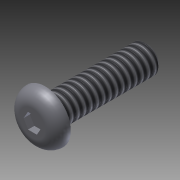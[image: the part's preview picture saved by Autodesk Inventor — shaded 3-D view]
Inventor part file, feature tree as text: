
AUTODESK INVENTOR PART (.ipt)
format: ipt  version: 2012 (Build 160160000, 160)  size: 116,736 bytes
history: native  units: in
note: dims shown in document units (in); Inventor stores cm internally (conversion verified against a paired STEP export)
features: extrude x3, sketch x1, thread x1, chamfer x1, fillet x1
ambient origin geometry x8: Origin, YZ Plane, XZ Plane, XY Plane, X Axis, Y Axis, Z Axis, Center Point
bodies: Solid1 (feature_tree)
feature tree (7):
  sketch  "Sketch1"  dims[d0=0.136in d1=0.25in d2=0.075in d3=0.5in d4=0.0in d5=0.0625in d6=0.0in d7=0.0312in d8=0.0in d9=1.0in d10=0.0in d11=0.0156in d12=0.125in d13=45.0deg d14=0.0625in]
  extrude  "Extrusion1"  Depth=0.25in
  extrude  "Extrusion2"  Depth=0.075in
  extrude  "Extrusion3"  Depth=0.5in TaperAngle=0.0deg
  thread  "Thread1"  [1 undecoded]
  chamfer  "Chamfer1"  Distance=0.0312in
  fillet  "Fillet1"  Radius=1.0in
note: 1 required parameter value undecoded (feature->parameter linkage not recoverable at this tier; creation-order binding heuristic only, values carry confidence <= 0.55)
